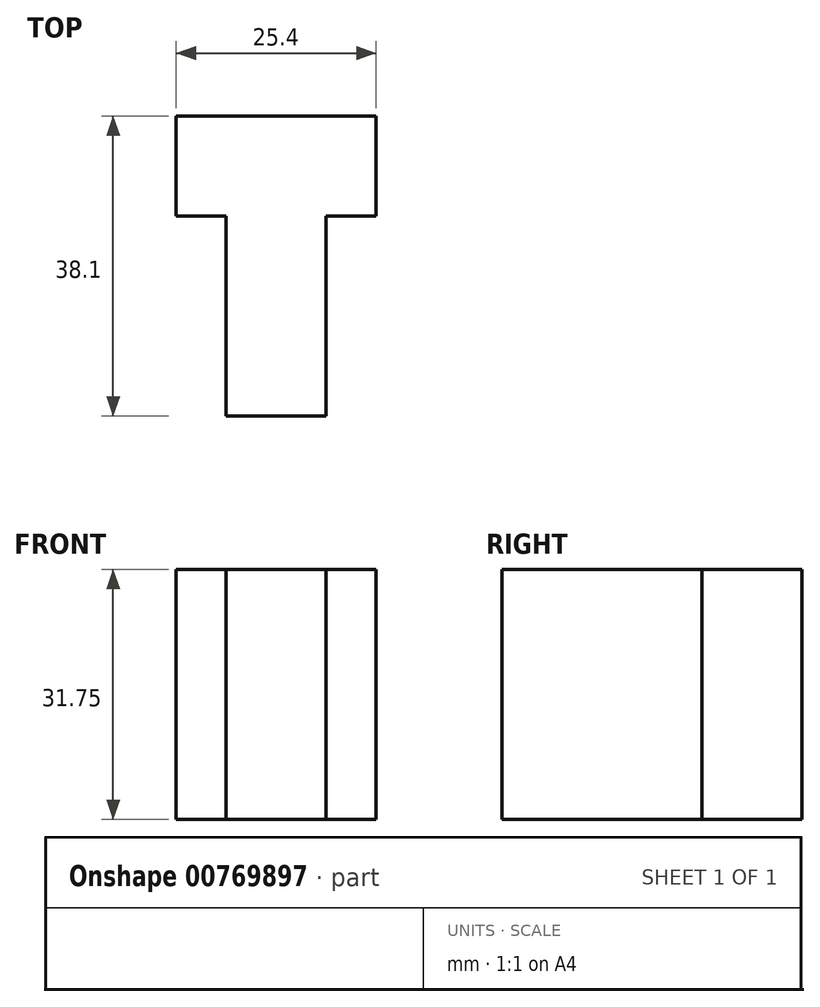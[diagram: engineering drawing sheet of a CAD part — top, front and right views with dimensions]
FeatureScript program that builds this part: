
annotation { "Feature Type Name" : "Feature", "Feature Type Description" : "" }
export const myFeature = defineFeature(function(context is Context, id is Id, definition is map)
    precondition{}
    {
        {
            var Q0;
            Q0=qCreatedBy(makeId("Top.planeOp"),FACE);
            var sketch = newSketch(context, id + "F0", { "sketchPlane" : qUnion([Q0])});
            skLineSegment(sketch, "E0", {"start": v(0, 0) * mm, "end": v(0, 25.4) * mm});
            skLineSegment(sketch, "E1", {"start": v(0, 25.4) * mm, "end": v(-6.35, 25.4) * mm});
            skLineSegment(sketch, "E2", {"start": v(-6.35, 25.4) * mm, "end": v(-6.35, 38.1) * mm});
            skLineSegment(sketch, "E3", {"start": v(-6.35, 38.1) * mm, "end": v(19.05, 38.1) * mm});
            skLineSegment(sketch, "E4", {"start": v(19.05, 38.1) * mm, "end": v(19.05, 25.4) * mm});
            skLineSegment(sketch, "E5", {"start": v(19.05, 25.4) * mm, "end": v(12.7, 25.4) * mm});
            skLineSegment(sketch, "E6", {"start": v(12.7, 25.4) * mm, "end": v(12.7, 0) * mm});
            skLineSegment(sketch, "E7", {"start": v(0, 0) * mm, "end": v(12.7, 0) * mm});
            skSolve(sketch);
        }
        {
            var Q0;
            Q0 = qSketchRegion(id + "F0", true);
            extrude(context, id + "F1", {"entities" : qUnion([Q0]), "depth" : 31.75 * mm, "offsetDistance" : 25.4 * mm});
        }
    });
